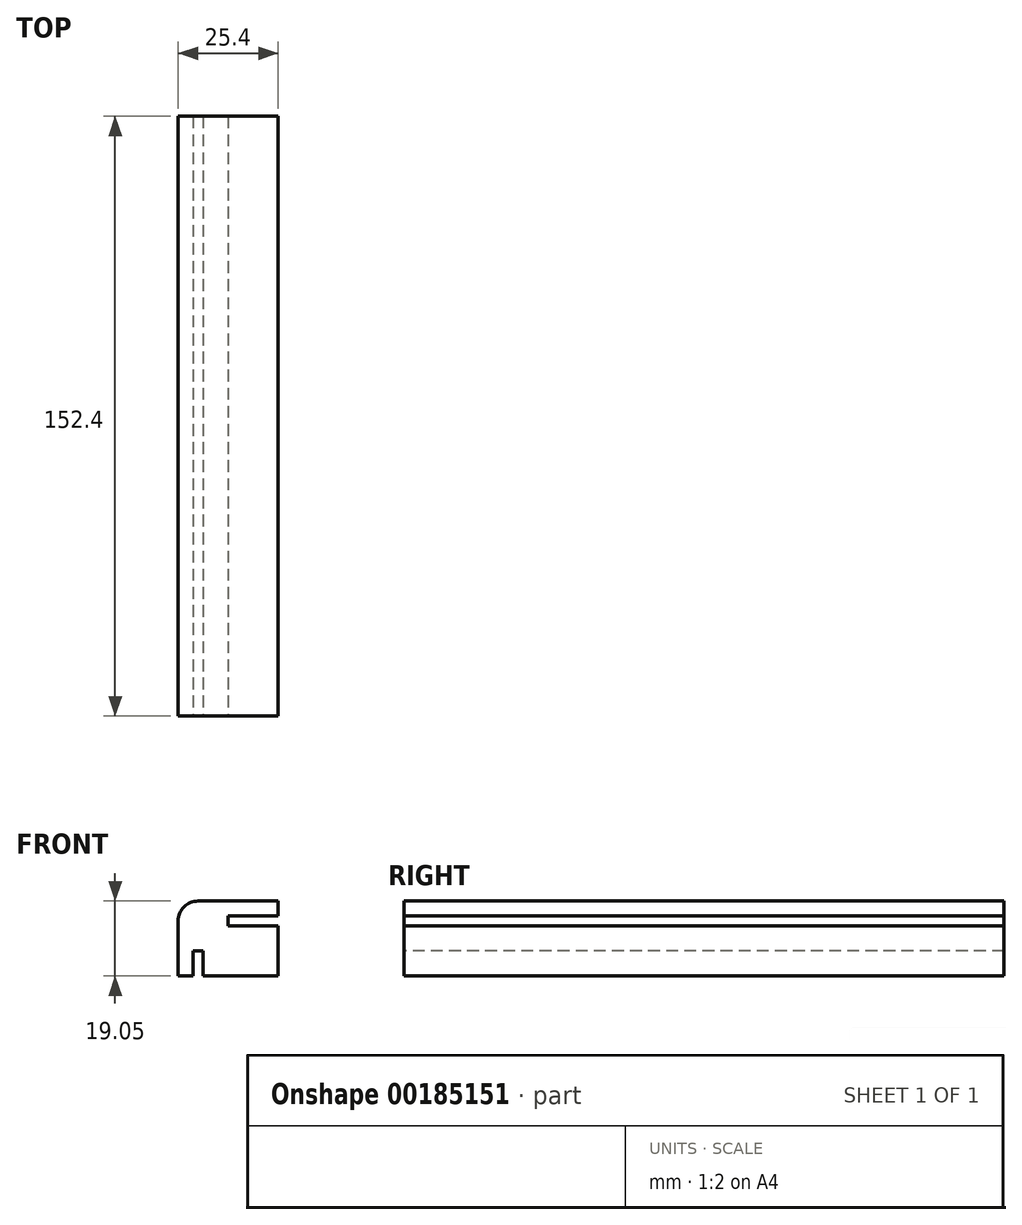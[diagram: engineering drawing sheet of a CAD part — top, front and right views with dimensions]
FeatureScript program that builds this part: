
annotation { "Feature Type Name" : "Feature", "Feature Type Description" : "" }
export const myFeature = defineFeature(function(context is Context, id is Id, definition is map)
    precondition{}
    {
        {
            var Q0;
            Q0=qCreatedBy(makeId("Top.planeOp"),FACE);
            var sketch = newSketch(context, id + "F0", { "sketchPlane" : qUnion([Q0])});
            skLineSegment(sketch, "E0.bottom", {"start": v(-12.7, 76.2) * mm, "end": v(12.7, 76.2) * mm});
            skLineSegment(sketch, "E0.top", {"start": v(-12.7, -76.2) * mm, "end": v(12.7, -76.2) * mm});
            skLineSegment(sketch, "E0.left", {"start": v(-12.7, 76.2) * mm, "end": v(-12.7, -76.2) * mm});
            skLineSegment(sketch, "E0.right", {"start": v(12.7, 76.2) * mm, "end": v(12.7, -76.2) * mm});
            skPoint(sketch, "E0.middle", {"position": v(0, 0) * mm});
            skSolve(sketch);
        }
        {
            var Q0;
            Q0=makeQuery(id+"F0.imprint","IMPRINT",FACE,{"disambiguationData":[TD([[makeQuery(id+"F0.imprint","IMPRINT",EDGE,{"derivedFrom":sQuery(id+"F0.wireOp",EDGE,"E0.bottom")}),-1.0]])]});
            extrude(context, id + "F1", {"entities" : qUnion([Q0]), "depth" : 19.05 * mm});
        }
        {
            var Q0;
            Q0=makeQuery(id+"F1.opExtrude","SWEPT_FACE",FACE,{"disambiguationData":[OSD([sQuery(id+"F0.wireOp",EDGE,"E0.top")])]});
            var sketch = newSketch(context, id + "F2", { "sketchPlane" : qUnion([Q0])});
            skLineSegment(sketch, "E1.bottom", {"start": v(12.7, 15.24) * mm, "end": v(0, 15.24) * mm});
            skLineSegment(sketch, "E1.top", {"start": v(12.7, 12.7) * mm, "end": v(0, 12.7) * mm});
            skLineSegment(sketch, "E1.left", {"start": v(12.7, 15.24) * mm, "end": v(12.7, 12.7) * mm});
            skLineSegment(sketch, "E1.right", {"start": v(0, 15.24) * mm, "end": v(0, 12.7) * mm});
            skLineSegment(sketch, "E2.bottom", {"start": v(-6.35, 0) * mm, "end": v(-8.89, 0) * mm});
            skLineSegment(sketch, "E2.top", {"start": v(-6.35, 6.35) * mm, "end": v(-8.89, 6.35) * mm});
            skLineSegment(sketch, "E2.left", {"start": v(-6.35, 0) * mm, "end": v(-6.35, 6.35) * mm});
            skLineSegment(sketch, "E2.right", {"start": v(-8.89, 0) * mm, "end": v(-8.89, 6.35) * mm});
            skSolve(sketch);
        }
        {
            var Q0;
            Q0=makeQuery(id+"F2.imprint","IMPRINT",FACE,{"disambiguationData":[TD([[makeQuery(id+"F2.imprint","IMPRINT",EDGE,{"derivedFrom":sQuery(id+"F2.wireOp",EDGE,"E1.bottom")}),1.0]])]});
            var Q1;
            Q1=makeQuery(id+"F2.imprint","IMPRINT",FACE,{"disambiguationData":[TD([[makeQuery(id+"F2.imprint","IMPRINT",EDGE,{"derivedFrom":sQuery(id+"F2.wireOp",EDGE,"E2.bottom")}),1.0]])]});
            extrude(context, id + "F3", {"entities" : qUnion([Q0, Q1]), "operationType" : NewBodyOperationType.REMOVE, "oppositeDirection" : true, "depth" : 177.8 * mm});
        }
        {
            var Q0;
            Q0=makeQuery(id+"F1.opExtrude","CAP_EDGE",EDGE,{"disambiguationData":[OSD([sQuery(id+"F0.wireOp",EDGE,"E0.left")])],"isStart":false});
            fillet(context, id + "F4", {"entities" : qUnion([Q0]), "radius" : 5.08 * mm, "tangentPropagation" : true, "allowEdgeOverflow" : false});
        }
    });
